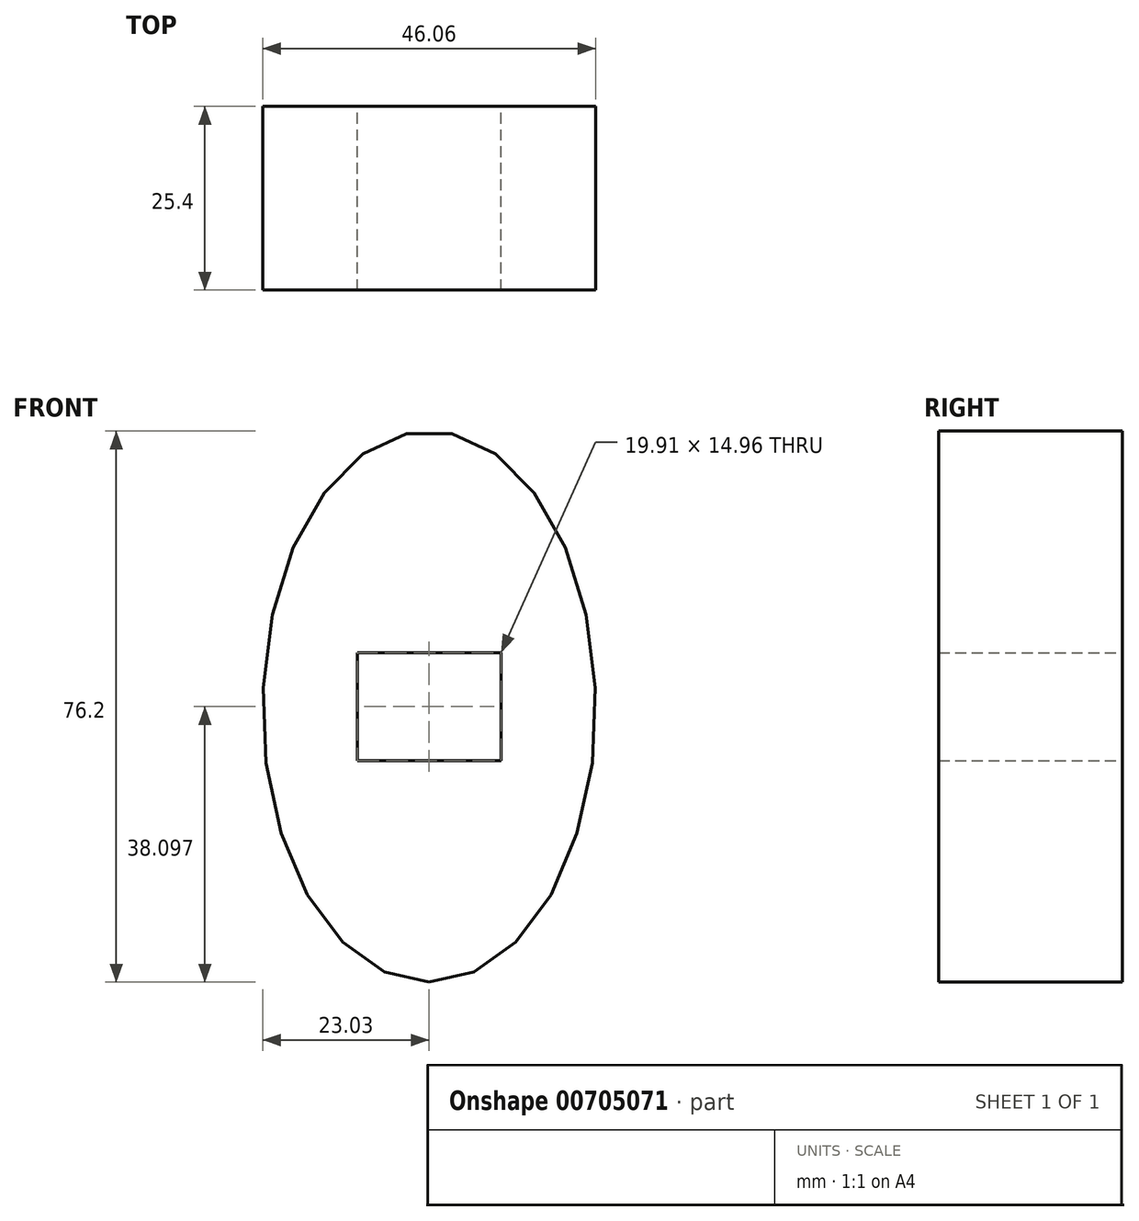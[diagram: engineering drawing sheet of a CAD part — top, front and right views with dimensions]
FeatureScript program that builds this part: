
annotation { "Feature Type Name" : "Feature", "Feature Type Description" : "" }
export const myFeature = defineFeature(function(context is Context, id is Id, definition is map)
    precondition{}
    {
        {
            var Q0;
            Q0=qCreatedBy(makeId("Front.planeOp"),FACE);
            var sketch = newSketch(context, id + "F0", { "sketchPlane" : qUnion([Q0])});
            skEllipse(sketch, "E0", {"center": v(0, 22.8) * mm, "majorRadius": 38.1 * mm, "minorRadius": 23.03 * mm, "majorAxis": v(0, -1)});
            skPoint(sketch, "E1.centerSnap0", {"position": v(0, -15.3) * mm});
            skLineSegment(sketch, "E2.bottom", {"start": v(-9.96, 30.29) * mm, "end": v(9.96, 30.29) * mm});
            skLineSegment(sketch, "E2.top", {"start": v(-9.96, 15.33) * mm, "end": v(9.96, 15.33) * mm});
            skLineSegment(sketch, "E2.left", {"start": v(-9.96, 30.29) * mm, "end": v(-9.96, 15.33) * mm});
            skLineSegment(sketch, "E2.right", {"start": v(9.96, 30.29) * mm, "end": v(9.96, 15.33) * mm});
            skSolve(sketch);
        }
        {
            var Q0;
            Q0=makeQuery(id+"F0.imprint","IMPRINT",FACE,{"disambiguationData":[TD([[makeQuery(id+"F0.imprint","IMPRINT",EDGE,{"derivedFrom":sQuery(id+"F0.wireOp",EDGE,"E0")}),1.0]])]});
            extrude(context, id + "F1", {"entities" : qUnion([Q0]), "depth" : 25.4 * mm, "offsetDistance" : 25.4 * mm});
        }
    });
